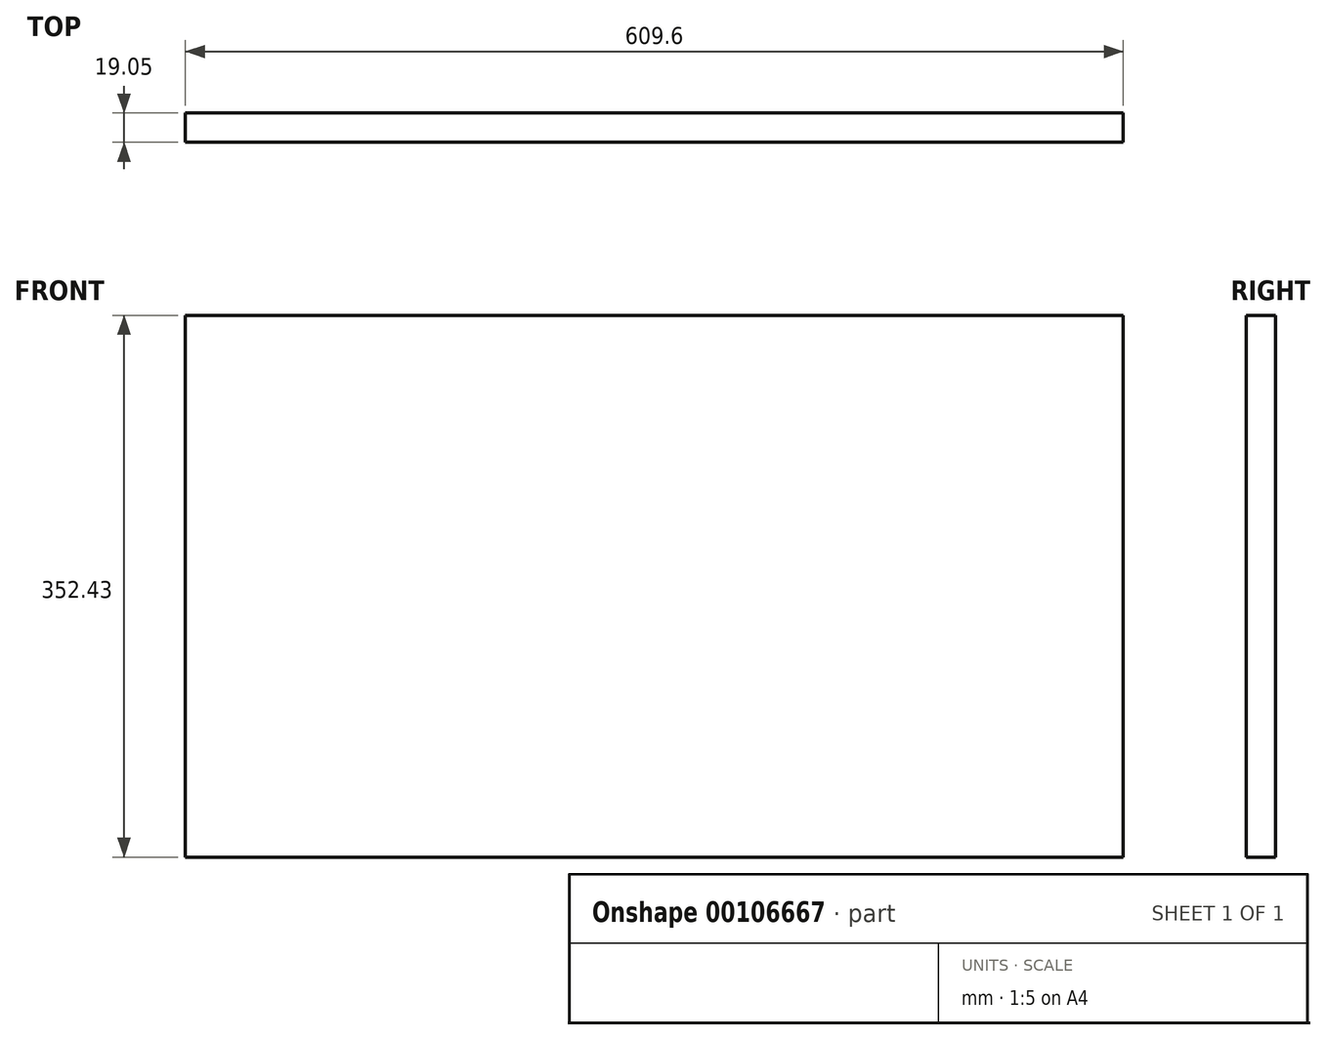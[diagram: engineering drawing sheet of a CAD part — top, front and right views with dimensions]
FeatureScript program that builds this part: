
annotation { "Feature Type Name" : "Feature", "Feature Type Description" : "" }
export const myFeature = defineFeature(function(context is Context, id is Id, definition is map)
    precondition{}
    {
        {
            var Q0;
            Q0=qCreatedBy(makeId("Front.planeOp"),FACE);
            var sketch = newSketch(context, id + "F0", { "sketchPlane" : qUnion([Q0])});
            skLineSegment(sketch, "E0.bottom", {"start": v(0, 0) * mm, "end": v(609.6, 0) * mm});
            skLineSegment(sketch, "E0.top", {"start": v(0, 352.43) * mm, "end": v(609.6, 352.43) * mm});
            skLineSegment(sketch, "E0.left", {"start": v(0, 0) * mm, "end": v(0, 352.42) * mm});
            skLineSegment(sketch, "E0.right", {"start": v(609.6, 0) * mm, "end": v(609.6, 352.43) * mm});
            skSolve(sketch);
        }
        {
            var Q0;
            Q0=makeQuery(id+"F0.imprint","IMPRINT",FACE,{"disambiguationData":[TD([[makeQuery(id+"F0.imprint","IMPRINT",EDGE,{"derivedFrom":sQuery(id+"F0.wireOp",EDGE,"E0.bottom")}),1.0]])]});
            extrude(context, id + "F1", {"entities" : qUnion([Q0]), "depth" : 19.05 * mm});
        }
    });
